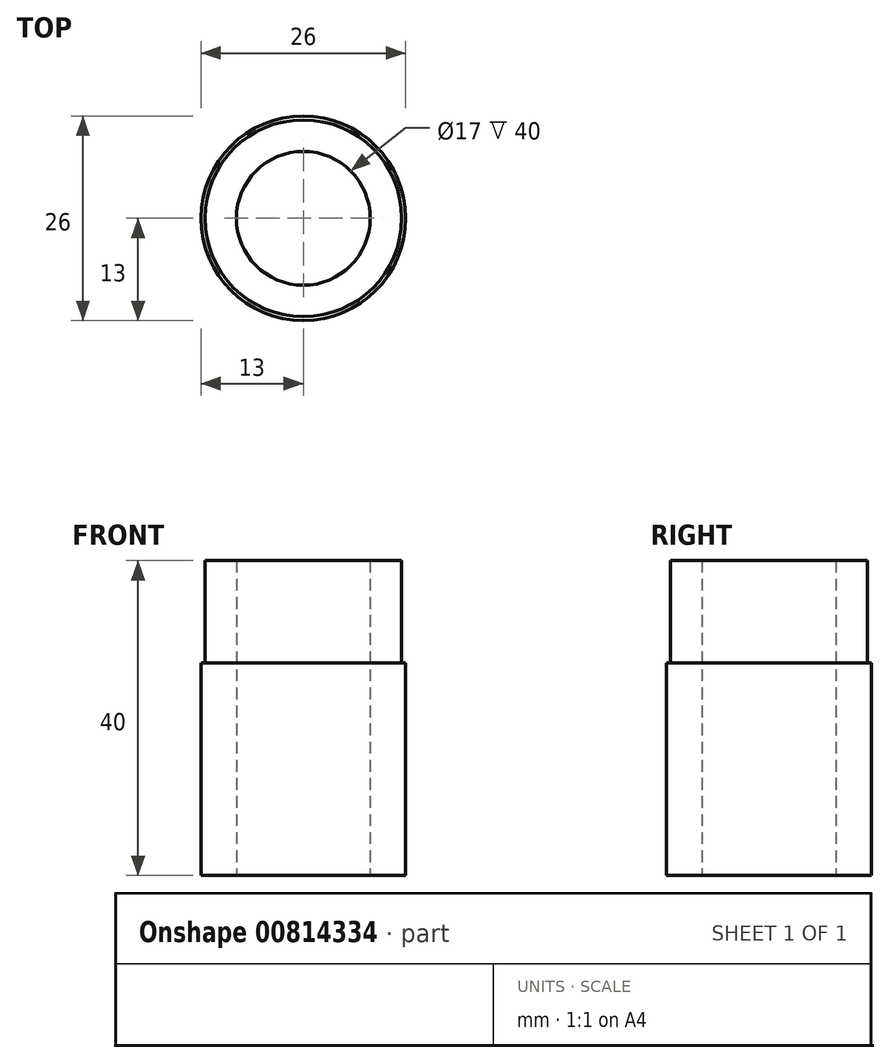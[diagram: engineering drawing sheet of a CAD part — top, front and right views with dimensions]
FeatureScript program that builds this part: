
annotation { "Feature Type Name" : "Feature", "Feature Type Description" : "" }
export const myFeature = defineFeature(function(context is Context, id is Id, definition is map)
    precondition{}
    {
        {
            var Q0;
            Q0=qCreatedBy(makeId("Top.planeOp"),FACE);
            var sketch = newSketch(context, id + "F0", { "sketchPlane" : qUnion([Q0])});
            skCircle(sketch, "E0", {"center": v(0, 0) * mm, "radius": 8.5 * mm});
            skCircle(sketch, "E1", {"center": v(0, 0) * mm, "radius": 12.5 * mm});
            skCircle(sketch, "E2", {"center": v(0, 0) * mm, "radius": 13 * mm});
            skSolve(sketch);
        }
        {
            var Q0;
            Q0=makeQuery(id+"F0.imprint","IMPRINT",FACE,{"disambiguationData":[TD([[makeQuery(id+"F0.imprint","IMPRINT",EDGE,{"derivedFrom":sQuery(id+"F0.wireOp",EDGE,"E0")}),-1.0]])]});
            extrude(context, id + "F1", {"entities" : qUnion([Q0]), "depth" : 13 * mm, "offsetDistance" : 25 * mm});
        }
        {
            var Q0;
            Q0 = qSketchRegion(id + "F0", true);
            var Q1;
            Q1=makeQuery(id+"F1.opExtrude","CAP_FACE",FACE,{"disambiguationData":[OSD([sQuery(id+"F0.wireOp",EDGE,"E0"),sQuery(id+"F0.wireOp",EDGE,"E1")])],"isStart":true});
            extrude(context, id + "F2", {"entities" : qUnion([Q0, Q1]), "operationType" : NewBodyOperationType.ADD, "oppositeDirection" : true, "depth" : 27 * mm, "offsetDistance" : 25 * mm});
        }
    });
